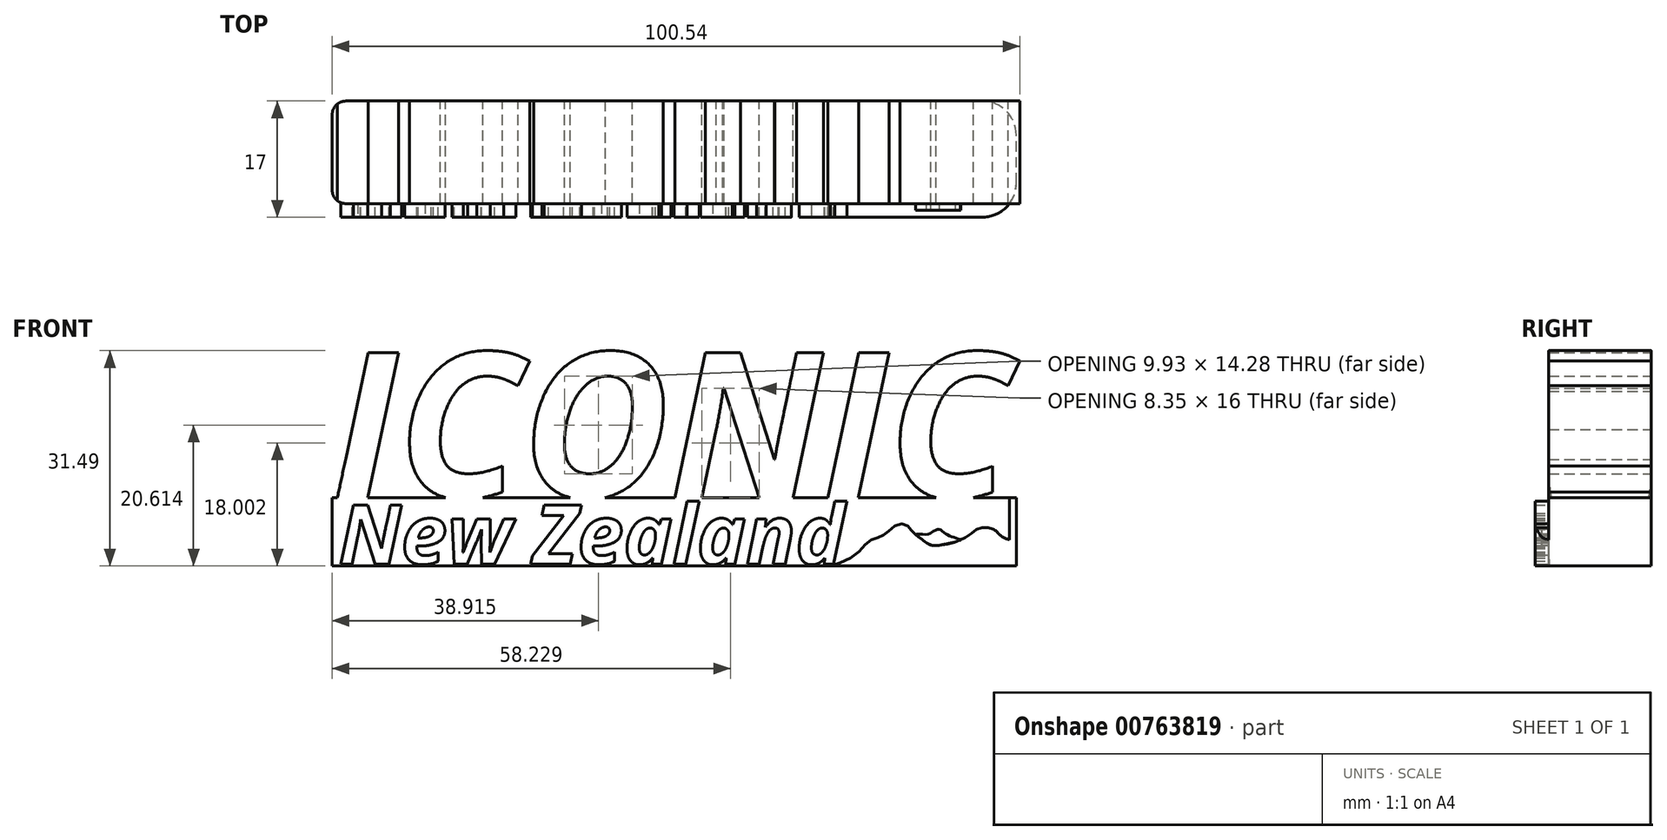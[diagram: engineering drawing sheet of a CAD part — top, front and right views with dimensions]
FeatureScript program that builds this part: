
annotation { "Feature Type Name" : "Feature", "Feature Type Description" : "" }
export const myFeature = defineFeature(function(context is Context, id is Id, definition is map)
    precondition{}
    {
        {
            var Q0;
            Q0=qCreatedBy(makeId("Front.planeOp"),FACE);
            var sketch = newSketch(context, id + "F0", { "sketchPlane" : qUnion([Q0])});
            skLineSegment(sketch, "E0.bottom", {"start": v(-50, 5) * mm, "end": v(50, 5) * mm});
            skLineSegment(sketch, "E0.top", {"start": v(-50, -5) * mm, "end": v(50, -5) * mm});
            skLineSegment(sketch, "E0.left", {"start": v(-50, 5) * mm, "end": v(-50, -5) * mm});
            skLineSegment(sketch, "E0.right", {"start": v(50, 5) * mm, "end": v(50, -5) * mm});
            skPoint(sketch, "E0.middle", {"position": v(0, 0) * mm});
            skText(sketch, "E1", { "text": "ICONIC", "fontName": "OpenSans-BoldItalic.ttf"});
            const initialGuessF0  = {"E1": [-0.05, 0.005, 1, 0, 0.02134]};
            skSetInitialGuess(sketch, initialGuessF0);
            skSolve(sketch);
        }
        {
            var Q0;
            Q0 = qSketchRegion(id + "F0", true);
            extrude(context, id + "F1", {"entities" : qUnion([Q0]), "depth" : 15 * mm, "offsetDistance" : 25 * mm});
        }
        {
            var Q0;
            Q0=makeQuery(id+"F1.opExtrude","CAP_FACE",FACE,{"disambiguationData":[OSD([sQuery(id+"F0.wireOp",EDGE,"E0.bottom"),sQuery(id+"F0.wireOp",EDGE,"E0.top"),sQuery(id+"F0.wireOp",EDGE,"E0.left"),sQuery(id+"F0.wireOp",EDGE,"E0.right"),sQuery(id+"F0.wireOp",EDGE,"E1.sketch_text.stroke-0"),sQuery(id+"F0.wireOp",EDGE,"E1.sketch_text.stroke-1"),sQuery(id+"F0.wireOp",EDGE,"E1.sketch_text.stroke-2"),sQuery(id+"F0.wireOp",EDGE,"E1.sketch_text.stroke-4"),sQuery(id+"F0.wireOp",EDGE,"E1.sketch_text.stroke-5"),sQuery(id+"F0.wireOp",EDGE,"E1.sketch_text.stroke-6"),sQuery(id+"F0.wireOp",EDGE,"E1.sketch_text.stroke-7"),sQuery(id+"F0.wireOp",EDGE,"E1.sketch_text.stroke-8"),sQuery(id+"F0.wireOp",EDGE,"E1.sketch_text.stroke-9"),sQuery(id+"F0.wireOp",EDGE,"E1.sketch_text.stroke-10"),sQuery(id+"F0.wireOp",EDGE,"E1.sketch_text.stroke-11"),sQuery(id+"F0.wireOp",EDGE,"E1.sketch_text.stroke-12"),sQuery(id+"F0.wireOp",EDGE,"E1.sketch_text.stroke-13"),sQuery(id+"F0.wireOp",EDGE,"E1.sketch_text.stroke-14"),sQuery(id+"F0.wireOp",EDGE,"E1.sketch_text.stroke-15"),sQuery(id+"F0.wireOp",EDGE,"E1.sketch_text.stroke-16"),sQuery(id+"F0.wireOp",EDGE,"E1.sketch_text.stroke-17"),sQuery(id+"F0.wireOp",EDGE,"E1.sketch_text.stroke-18"),sQuery(id+"F0.wireOp",EDGE,"E1.sketch_text.stroke-19"),sQuery(id+"F0.wireOp",EDGE,"E1.sketch_text.stroke-20"),sQuery(id+"F0.wireOp",EDGE,"E1.sketch_text.stroke-21"),sQuery(id+"F0.wireOp",EDGE,"E1.sketch_text.stroke-22"),sQuery(id+"F0.wireOp",EDGE,"E1.sketch_text.stroke-23"),sQuery(id+"F0.wireOp",EDGE,"E1.sketch_text.stroke-24"),sQuery(id+"F0.wireOp",EDGE,"E1.sketch_text.stroke-25"),sQuery(id+"F0.wireOp",EDGE,"E1.sketch_text.stroke-26"),sQuery(id+"F0.wireOp",EDGE,"E1.sketch_text.stroke-27"),sQuery(id+"F0.wireOp",EDGE,"E1.sketch_text.stroke-28"),sQuery(id+"F0.wireOp",EDGE,"E1.sketch_text.stroke-29"),sQuery(id+"F0.wireOp",EDGE,"E1.sketch_text.stroke-30"),sQuery(id+"F0.wireOp",EDGE,"E1.sketch_text.stroke-31"),sQuery(id+"F0.wireOp",EDGE,"E1.sketch_text.stroke-32"),sQuery(id+"F0.wireOp",EDGE,"E1.sketch_text.stroke-33"),sQuery(id+"F0.wireOp",EDGE,"E1.sketch_text.stroke-34"),sQuery(id+"F0.wireOp",EDGE,"E1.sketch_text.stroke-35"),sQuery(id+"F0.wireOp",EDGE,"E1.sketch_text.stroke-36"),sQuery(id+"F0.wireOp",EDGE,"E1.sketch_text.stroke-37"),sQuery(id+"F0.wireOp",EDGE,"E1.sketch_text.stroke-38"),sQuery(id+"F0.wireOp",EDGE,"E1.sketch_text.stroke-39"),sQuery(id+"F0.wireOp",EDGE,"E1.sketch_text.stroke-40"),sQuery(id+"F0.wireOp",EDGE,"E1.sketch_text.stroke-41"),sQuery(id+"F0.wireOp",EDGE,"E1.sketch_text.stroke-43"),sQuery(id+"F0.wireOp",EDGE,"E1.sketch_text.stroke-44"),sQuery(id+"F0.wireOp",EDGE,"E1.sketch_text.stroke-45"),sQuery(id+"F0.wireOp",EDGE,"E1.sketch_text.stroke-46"),sQuery(id+"F0.wireOp",EDGE,"E1.sketch_text.stroke-47"),sQuery(id+"F0.wireOp",EDGE,"E1.sketch_text.stroke-49"),sQuery(id+"F0.wireOp",EDGE,"E1.sketch_text.stroke-50"),sQuery(id+"F0.wireOp",EDGE,"E1.sketch_text.stroke-51"),sQuery(id+"F0.wireOp",EDGE,"E1.sketch_text.stroke-52"),sQuery(id+"F0.wireOp",EDGE,"E1.sketch_text.stroke-53"),sQuery(id+"F0.wireOp",EDGE,"E1.sketch_text.stroke-54"),sQuery(id+"F0.wireOp",EDGE,"E1.sketch_text.stroke-55"),sQuery(id+"F0.wireOp",EDGE,"E1.sketch_text.stroke-56"),sQuery(id+"F0.wireOp",EDGE,"E1.sketch_text.stroke-57"),sQuery(id+"F0.wireOp",EDGE,"E1.sketch_text.stroke-58"),sQuery(id+"F0.wireOp",EDGE,"E1.sketch_text.stroke-59"),sQuery(id+"F0.wireOp",EDGE,"E1.sketch_text.stroke-61"),sQuery(id+"F0.wireOp",EDGE,"E1.sketch_text.stroke-62"),sQuery(id+"F0.wireOp",EDGE,"E1.sketch_text.stroke-63"),sQuery(id+"F0.wireOp",EDGE,"E1.sketch_text.stroke-64"),sQuery(id+"F0.wireOp",EDGE,"E1.sketch_text.stroke-65"),sQuery(id+"F0.wireOp",EDGE,"E1.sketch_text.stroke-66"),sQuery(id+"F0.wireOp",EDGE,"E1.sketch_text.stroke-67"),sQuery(id+"F0.wireOp",EDGE,"E1.sketch_text.stroke-68"),sQuery(id+"F0.wireOp",EDGE,"E1.sketch_text.stroke-69"),sQuery(id+"F0.wireOp",EDGE,"E1.sketch_text.stroke-70"),sQuery(id+"F0.wireOp",EDGE,"E1.sketch_text.stroke-71"),sQuery(id+"F0.wireOp",EDGE,"E1.sketch_text.stroke-72"),sQuery(id+"F0.wireOp",EDGE,"E1.sketch_text.stroke-73"),sQuery(id+"F0.wireOp",EDGE,"E1.sketch_text.stroke-74"),sQuery(id+"F0.wireOp",EDGE,"E1.sketch_text.stroke-75"),sQuery(id+"F0.wireOp",EDGE,"E1.sketch_text.stroke-76"),sQuery(id+"F0.wireOp",EDGE,"E1.sketch_text.stroke-77"),sQuery(id+"F0.wireOp",EDGE,"E1.sketch_text.stroke-78")])],"isStart":false});
            var sketch = newSketch(context, id + "F2", { "sketchPlane" : qUnion([Q0])});
            skText(sketch, "E2", { "text": "New Zealand", "fontName": "OpenSans-BoldItalic.ttf"});
            const initialGuessF2  = {"E2": [-0.04902, -0.00471, 1, 0, 0.00867]};
            skSetInitialGuess(sketch, initialGuessF2);
            skSolve(sketch);
        }
        {
            var Q0;
            Q0 = qSketchRegion(id + "F2", true);
            extrude(context, id + "F3", {"entities" : qUnion([Q0]), "operationType" : NewBodyOperationType.ADD, "depth" : 2 * mm, "offsetDistance" : 25 * mm});
        }
        {
            var Q0;
            {var subQ0=sQuery(id+"F0.wireOp",EDGE,"E1.sketch_text.stroke-34");var subQ1=sQuery(id+"F0.wireOp",EDGE,"E1.sketch_text.stroke-33");var subQ2=sQuery(id+"F0.wireOp",EDGE,"E1.sketch_text.stroke-32");var subQ3=sQuery(id+"F0.wireOp",EDGE,"E1.sketch_text.stroke-55");var subQ4=sQuery(id+"F0.wireOp",EDGE,"E1.sketch_text.stroke-31");var subQ5=sQuery(id+"F0.wireOp",EDGE,"E1.sketch_text.stroke-54");var subQ6=sQuery(id+"F0.wireOp",EDGE,"E1.sketch_text.stroke-30");var subQ7=sQuery(id+"F0.wireOp",EDGE,"E1.sketch_text.stroke-53");var subQ8=sQuery(id+"F0.wireOp",EDGE,"E1.sketch_text.stroke-29");var subQ9=sQuery(id+"F0.wireOp",EDGE,"E1.sketch_text.stroke-52");var subQ10=sQuery(id+"F0.wireOp",EDGE,"E1.sketch_text.stroke-28");var subQ11=sQuery(id+"F0.wireOp",EDGE,"E1.sketch_text.stroke-51");var subQ12=sQuery(id+"F0.wireOp",EDGE,"E1.sketch_text.stroke-27");var subQ13=sQuery(id+"F0.wireOp",EDGE,"E1.sketch_text.stroke-17");var subQ14=sQuery(id+"F0.wireOp",EDGE,"E1.sketch_text.stroke-26");var subQ15=sQuery(id+"F0.wireOp",EDGE,"E1.sketch_text.stroke-50");var subQ16=sQuery(id+"F0.wireOp",EDGE,"E1.sketch_text.stroke-16");var subQ17=sQuery(id+"F0.wireOp",EDGE,"E1.sketch_text.stroke-25");var subQ18=sQuery(id+"F0.wireOp",EDGE,"E1.sketch_text.stroke-49");var subQ19=sQuery(id+"F0.wireOp",EDGE,"E1.sketch_text.stroke-24");var subQ20=sQuery(id+"F0.wireOp",EDGE,"E1.sketch_text.stroke-47");var subQ21=sQuery(id+"F0.wireOp",EDGE,"E1.sketch_text.stroke-14");var subQ22=sQuery(id+"F0.wireOp",EDGE,"E1.sketch_text.stroke-23");var subQ23=sQuery(id+"F0.wireOp",EDGE,"E1.sketch_text.stroke-46");var subQ24=sQuery(id+"F0.wireOp",EDGE,"E1.sketch_text.stroke-13");var subQ25=sQuery(id+"F0.wireOp",EDGE,"E1.sketch_text.stroke-22");var subQ26=sQuery(id+"F0.wireOp",EDGE,"E1.sketch_text.stroke-45");var subQ27=sQuery(id+"F0.wireOp",EDGE,"E1.sketch_text.stroke-12");var subQ28=sQuery(id+"F0.wireOp",EDGE,"E1.sketch_text.stroke-21");var subQ29=sQuery(id+"F0.wireOp",EDGE,"E1.sketch_text.stroke-44");var subQ30=sQuery(id+"F0.wireOp",EDGE,"E0.top");var subQ31=sQuery(id+"F0.wireOp",EDGE,"E0.right");var subQ32=sQuery(id+"F0.wireOp",EDGE,"E0.bottom");var subQ33=sQuery(id+"F0.wireOp",EDGE,"E1.sketch_text.stroke-68");var subQ35=sQuery(id+"F0.wireOp",EDGE,"E1.sketch_text.stroke-59");var subQ36=sQuery(id+"F0.wireOp",EDGE,"E1.sketch_text.stroke-69");var subQ37=sQuery(id+"F0.wireOp",EDGE,"E1.sketch_text.stroke-56");var subQ39=sQuery(id+"F0.wireOp",EDGE,"E1.sketch_text.stroke-57");var subQ40=sQuery(id+"F0.wireOp",EDGE,"E1.sketch_text.stroke-43");var subQ42=sQuery(id+"F0.wireOp",EDGE,"E0.left");var subQ43=sQuery(id+"F0.wireOp",EDGE,"E1.sketch_text.stroke-35");var subQ45=sQuery(id+"F0.wireOp",EDGE,"E1.sketch_text.stroke-0");var subQ46=sQuery(id+"F0.wireOp",EDGE,"E1.sketch_text.stroke-11");var subQ47=sQuery(id+"F0.wireOp",EDGE,"E1.sketch_text.stroke-20");var subQ48=sQuery(id+"F0.wireOp",EDGE,"E1.sketch_text.stroke-2");var subQ49=sQuery(id+"F0.wireOp",EDGE,"E1.sketch_text.stroke-1");var subQ50=sQuery(id+"F0.wireOp",EDGE,"E1.sketch_text.stroke-4");var subQ51=sQuery(id+"F0.wireOp",EDGE,"E1.sketch_text.stroke-5");var subQ52=sQuery(id+"F0.wireOp",EDGE,"E1.sketch_text.stroke-6");var subQ53=sQuery(id+"F0.wireOp",EDGE,"E1.sketch_text.stroke-15");var subQ54=sQuery(id+"F0.wireOp",EDGE,"E1.sketch_text.stroke-37");var subQ55=sQuery(id+"F0.wireOp",EDGE,"E1.sketch_text.stroke-7");var subQ56=sQuery(id+"F0.wireOp",EDGE,"E1.sketch_text.stroke-8");var subQ57=sQuery(id+"F0.wireOp",EDGE,"E1.sketch_text.stroke-9");var subQ58=sQuery(id+"F0.wireOp",EDGE,"E1.sketch_text.stroke-18");var subQ59=sQuery(id+"F0.wireOp",EDGE,"E1.sketch_text.stroke-40");var subQ60=sQuery(id+"F0.wireOp",EDGE,"E1.sketch_text.stroke-10");var subQ61=sQuery(id+"F0.wireOp",EDGE,"E1.sketch_text.stroke-19");var subQ62=sQuery(id+"F0.wireOp",EDGE,"E1.sketch_text.stroke-41");var subQ63=sQuery(id+"F0.wireOp",EDGE,"E1.sketch_text.stroke-36");var subQ64=sQuery(id+"F0.wireOp",EDGE,"E1.sketch_text.stroke-38");var subQ65=sQuery(id+"F0.wireOp",EDGE,"E1.sketch_text.stroke-39");var subQ66=sQuery(id+"F0.wireOp",EDGE,"E1.sketch_text.stroke-65");var subQ67=sQuery(id+"F0.wireOp",EDGE,"E1.sketch_text.stroke-66");var subQ68=sQuery(id+"F0.wireOp",EDGE,"E1.sketch_text.stroke-67");var subQ69=sQuery(id+"F0.wireOp",EDGE,"E1.sketch_text.stroke-70");var subQ70=sQuery(id+"F0.wireOp",EDGE,"E1.sketch_text.stroke-71");var subQ71=sQuery(id+"F0.wireOp",EDGE,"E1.sketch_text.stroke-72");var subQ72=sQuery(id+"F0.wireOp",EDGE,"E1.sketch_text.stroke-73");var subQ73=sQuery(id+"F0.wireOp",EDGE,"E1.sketch_text.stroke-74");var subQ74=sQuery(id+"F0.wireOp",EDGE,"E1.sketch_text.stroke-75");var subQ75=sQuery(id+"F0.wireOp",EDGE,"E1.sketch_text.stroke-76");var subQ76=sQuery(id+"F0.wireOp",EDGE,"E1.sketch_text.stroke-77");var subQ77=sQuery(id+"F0.wireOp",EDGE,"E1.sketch_text.stroke-78");var subQ78=sQuery(id+"F0.wireOp",EDGE,"E1.sketch_text.stroke-58");var subQ79=sQuery(id+"F0.wireOp",EDGE,"E1.sketch_text.stroke-61");var subQ80=sQuery(id+"F0.wireOp",EDGE,"E1.sketch_text.stroke-62");var subQ81=sQuery(id+"F0.wireOp",EDGE,"E1.sketch_text.stroke-63");var subQ82=sQuery(id+"F0.wireOp",EDGE,"E1.sketch_text.stroke-64");Q0=makeQuery(id+"F3.boolean.opBoolean","SPLIT",FACE,{"disambiguationData":[TD([makeQuery(id+"F1.opExtrude","SWEPT_FACE",FACE,{"disambiguationData":[OSD([subQ30])]})])],"derivedFrom":makeQuery(id+"F1.opExtrude","CAP_FACE",FACE,{"disambiguationData":[OSD([subQ32,subQ30,subQ42,subQ31,subQ45,subQ49,subQ48,subQ50,subQ51,subQ52,subQ55,subQ56,subQ57,subQ60,subQ46,subQ27,subQ24,subQ21,subQ53,subQ16,subQ13,subQ58,subQ61,subQ47,subQ28,subQ25,subQ22,subQ19,subQ17,subQ14,subQ12,subQ10,subQ8,subQ6,subQ4,subQ2,subQ1,subQ0,subQ43,subQ63,subQ54,subQ64,subQ65,subQ59,subQ62,subQ40,subQ29,subQ26,subQ23,subQ20,subQ18,subQ15,subQ11,subQ9,subQ7,subQ5,subQ3,subQ37,subQ39,subQ78,subQ35,subQ79,subQ80,subQ81,subQ82,subQ66,subQ67,subQ68,subQ33,subQ36,subQ69,subQ70,subQ71,subQ72,subQ73,subQ74,subQ75,subQ76,subQ77])],"isStart":false})});}
            var sketch = newSketch(context, id + "F4", { "sketchPlane" : qUnion([Q0])});
            skFitSpline(sketch, "E3", {"points": [v(22.82, -5) * mm, v(26.5, -3.3) * mm, v(28.51, -1.35) * mm, v(30.03, -0.76) * mm, v(31.19, 0) * mm, v(32.84, 1.12) * mm, v(34.25, 0.73) * mm, v(34.78, 0) * mm, v(36.07, -1.02) * mm, v(37.39, -1.91) * mm, v(39, -1.94) * mm, v(41.84, -1.22) * mm, v(43.79, 0) * mm, v(44.71, 0.56) * mm, v(46.76, 0.3) * mm, v(47.81, -0.66) * mm, v(50, -1.38) * mm], "startDerivative": vector(35.27, 6.8) * mm, "endDerivative": vector(35.57, -7.54) * mm});
            skLineSegment(sketch, "E4", {"start": v(22.82, -5) * mm, "end": v(50, -5) * mm});
            skLineSegment(sketch, "E5", {"start": v(50, -5) * mm, "end": v(50, -1.38) * mm});
            skSolve(sketch);
        }
        {
            var Q0;
            Q0 = qSketchRegion(id + "F4", true);
            extrude(context, id + "F5", {"entities" : qUnion([Q0]), "operationType" : NewBodyOperationType.ADD, "depth" : 2 * mm, "offsetDistance" : 25 * mm});
        }
        {
            var Q0;
            {var subQ0=sQuery(id+"F0.wireOp",EDGE,"E1.sketch_text.stroke-34");var subQ1=sQuery(id+"F0.wireOp",EDGE,"E1.sketch_text.stroke-33");var subQ2=sQuery(id+"F0.wireOp",EDGE,"E1.sketch_text.stroke-32");var subQ3=sQuery(id+"F0.wireOp",EDGE,"E1.sketch_text.stroke-55");var subQ4=sQuery(id+"F0.wireOp",EDGE,"E1.sketch_text.stroke-31");var subQ5=sQuery(id+"F0.wireOp",EDGE,"E1.sketch_text.stroke-54");var subQ6=sQuery(id+"F0.wireOp",EDGE,"E1.sketch_text.stroke-30");var subQ7=sQuery(id+"F0.wireOp",EDGE,"E1.sketch_text.stroke-53");var subQ8=sQuery(id+"F0.wireOp",EDGE,"E1.sketch_text.stroke-29");var subQ9=sQuery(id+"F0.wireOp",EDGE,"E1.sketch_text.stroke-52");var subQ10=sQuery(id+"F0.wireOp",EDGE,"E1.sketch_text.stroke-28");var subQ11=sQuery(id+"F0.wireOp",EDGE,"E1.sketch_text.stroke-51");var subQ12=sQuery(id+"F0.wireOp",EDGE,"E1.sketch_text.stroke-27");var subQ13=sQuery(id+"F0.wireOp",EDGE,"E1.sketch_text.stroke-17");var subQ14=sQuery(id+"F0.wireOp",EDGE,"E1.sketch_text.stroke-26");var subQ15=sQuery(id+"F0.wireOp",EDGE,"E1.sketch_text.stroke-50");var subQ16=sQuery(id+"F0.wireOp",EDGE,"E1.sketch_text.stroke-16");var subQ17=sQuery(id+"F0.wireOp",EDGE,"E1.sketch_text.stroke-25");var subQ18=sQuery(id+"F0.wireOp",EDGE,"E1.sketch_text.stroke-49");var subQ19=sQuery(id+"F0.wireOp",EDGE,"E1.sketch_text.stroke-24");var subQ20=sQuery(id+"F0.wireOp",EDGE,"E1.sketch_text.stroke-47");var subQ21=sQuery(id+"F0.wireOp",EDGE,"E1.sketch_text.stroke-14");var subQ22=sQuery(id+"F0.wireOp",EDGE,"E1.sketch_text.stroke-23");var subQ23=sQuery(id+"F0.wireOp",EDGE,"E1.sketch_text.stroke-46");var subQ24=sQuery(id+"F0.wireOp",EDGE,"E1.sketch_text.stroke-13");var subQ25=sQuery(id+"F0.wireOp",EDGE,"E1.sketch_text.stroke-22");var subQ26=sQuery(id+"F0.wireOp",EDGE,"E1.sketch_text.stroke-45");var subQ27=sQuery(id+"F0.wireOp",EDGE,"E1.sketch_text.stroke-12");var subQ28=sQuery(id+"F0.wireOp",EDGE,"E1.sketch_text.stroke-21");var subQ29=sQuery(id+"F0.wireOp",EDGE,"E1.sketch_text.stroke-44");var subQ30=sQuery(id+"F0.wireOp",EDGE,"E0.top");var subQ31=sQuery(id+"F0.wireOp",EDGE,"E0.right");var subQ32=sQuery(id+"F0.wireOp",EDGE,"E0.bottom");var subQ33=sQuery(id+"F0.wireOp",EDGE,"E1.sketch_text.stroke-68");var subQ35=sQuery(id+"F0.wireOp",EDGE,"E1.sketch_text.stroke-59");var subQ36=sQuery(id+"F0.wireOp",EDGE,"E1.sketch_text.stroke-69");var subQ37=sQuery(id+"F0.wireOp",EDGE,"E1.sketch_text.stroke-56");var subQ39=sQuery(id+"F0.wireOp",EDGE,"E1.sketch_text.stroke-57");var subQ40=sQuery(id+"F0.wireOp",EDGE,"E1.sketch_text.stroke-43");var subQ42=sQuery(id+"F0.wireOp",EDGE,"E0.left");var subQ43=sQuery(id+"F0.wireOp",EDGE,"E1.sketch_text.stroke-35");var subQ45=sQuery(id+"F0.wireOp",EDGE,"E1.sketch_text.stroke-0");var subQ46=sQuery(id+"F0.wireOp",EDGE,"E1.sketch_text.stroke-11");var subQ47=sQuery(id+"F0.wireOp",EDGE,"E1.sketch_text.stroke-20");var subQ48=sQuery(id+"F0.wireOp",EDGE,"E1.sketch_text.stroke-2");var subQ49=sQuery(id+"F0.wireOp",EDGE,"E1.sketch_text.stroke-1");var subQ50=sQuery(id+"F0.wireOp",EDGE,"E1.sketch_text.stroke-4");var subQ51=sQuery(id+"F0.wireOp",EDGE,"E1.sketch_text.stroke-5");var subQ52=sQuery(id+"F0.wireOp",EDGE,"E1.sketch_text.stroke-6");var subQ53=sQuery(id+"F0.wireOp",EDGE,"E1.sketch_text.stroke-15");var subQ54=sQuery(id+"F0.wireOp",EDGE,"E1.sketch_text.stroke-37");var subQ55=sQuery(id+"F0.wireOp",EDGE,"E1.sketch_text.stroke-7");var subQ56=sQuery(id+"F0.wireOp",EDGE,"E1.sketch_text.stroke-8");var subQ57=sQuery(id+"F0.wireOp",EDGE,"E1.sketch_text.stroke-9");var subQ58=sQuery(id+"F0.wireOp",EDGE,"E1.sketch_text.stroke-18");var subQ59=sQuery(id+"F0.wireOp",EDGE,"E1.sketch_text.stroke-40");var subQ60=sQuery(id+"F0.wireOp",EDGE,"E1.sketch_text.stroke-10");var subQ61=sQuery(id+"F0.wireOp",EDGE,"E1.sketch_text.stroke-19");var subQ62=sQuery(id+"F0.wireOp",EDGE,"E1.sketch_text.stroke-41");var subQ63=sQuery(id+"F0.wireOp",EDGE,"E1.sketch_text.stroke-36");var subQ64=sQuery(id+"F0.wireOp",EDGE,"E1.sketch_text.stroke-38");var subQ65=sQuery(id+"F0.wireOp",EDGE,"E1.sketch_text.stroke-39");var subQ66=sQuery(id+"F0.wireOp",EDGE,"E1.sketch_text.stroke-65");var subQ67=sQuery(id+"F0.wireOp",EDGE,"E1.sketch_text.stroke-66");var subQ68=sQuery(id+"F0.wireOp",EDGE,"E1.sketch_text.stroke-67");var subQ69=sQuery(id+"F0.wireOp",EDGE,"E1.sketch_text.stroke-70");var subQ70=sQuery(id+"F0.wireOp",EDGE,"E1.sketch_text.stroke-71");var subQ71=sQuery(id+"F0.wireOp",EDGE,"E1.sketch_text.stroke-72");var subQ72=sQuery(id+"F0.wireOp",EDGE,"E1.sketch_text.stroke-73");var subQ73=sQuery(id+"F0.wireOp",EDGE,"E1.sketch_text.stroke-74");var subQ74=sQuery(id+"F0.wireOp",EDGE,"E1.sketch_text.stroke-75");var subQ75=sQuery(id+"F0.wireOp",EDGE,"E1.sketch_text.stroke-76");var subQ76=sQuery(id+"F0.wireOp",EDGE,"E1.sketch_text.stroke-77");var subQ77=sQuery(id+"F0.wireOp",EDGE,"E1.sketch_text.stroke-78");var subQ78=sQuery(id+"F0.wireOp",EDGE,"E1.sketch_text.stroke-58");var subQ79=sQuery(id+"F0.wireOp",EDGE,"E1.sketch_text.stroke-61");var subQ80=sQuery(id+"F0.wireOp",EDGE,"E1.sketch_text.stroke-62");var subQ81=sQuery(id+"F0.wireOp",EDGE,"E1.sketch_text.stroke-63");var subQ82=sQuery(id+"F0.wireOp",EDGE,"E1.sketch_text.stroke-64");Q0=makeQuery(id+"F3.boolean.opBoolean","SPLIT",FACE,{"disambiguationData":[TD([makeQuery(id+"F1.opExtrude","SWEPT_FACE",FACE,{"disambiguationData":[OSD([subQ30])]})])],"derivedFrom":makeQuery(id+"F1.opExtrude","CAP_FACE",FACE,{"disambiguationData":[OSD([subQ32,subQ30,subQ42,subQ31,subQ45,subQ49,subQ48,subQ50,subQ51,subQ52,subQ55,subQ56,subQ57,subQ60,subQ46,subQ27,subQ24,subQ21,subQ53,subQ16,subQ13,subQ58,subQ61,subQ47,subQ28,subQ25,subQ22,subQ19,subQ17,subQ14,subQ12,subQ10,subQ8,subQ6,subQ4,subQ2,subQ1,subQ0,subQ43,subQ63,subQ54,subQ64,subQ65,subQ59,subQ62,subQ40,subQ29,subQ26,subQ23,subQ20,subQ18,subQ15,subQ11,subQ9,subQ7,subQ5,subQ3,subQ37,subQ39,subQ78,subQ35,subQ79,subQ80,subQ81,subQ82,subQ66,subQ67,subQ68,subQ33,subQ36,subQ69,subQ70,subQ71,subQ72,subQ73,subQ74,subQ75,subQ76,subQ77])],"isStart":false})});}
            var sketch = newSketch(context, id + "F6", { "sketchPlane" : qUnion([Q0])});
            skFitSpline(sketch, "E6", {"points": [v(35.27, -0.44) * mm, v(36.8, -0.4) * mm, v(37.77, 0) * mm, v(38.66, 0.35) * mm, v(39.27, 0) * mm, v(40.21, -0.59) * mm, v(41.46, -1) * mm, v(41.84, -1.22) * mm, v(38.77, -1.98) * mm, v(37.5, -1.95) * mm, v(35.27, -0.44) * mm]});
            skSolve(sketch);
        }
        {
            var Q0;
            Q0 = qSketchRegion(id + "F6", true);
            extrude(context, id + "F7", {"entities" : qUnion([Q0]), "operationType" : NewBodyOperationType.ADD, "depth" : 1 * mm, "offsetDistance" : 25 * mm});
        }
        {
            var Q0;
            Q0=makeQuery(id+"F5.opExtrude","CAP_EDGE",EDGE,{"disambiguationData":[OSD([sQuery(id+"F4.wireOp",EDGE,"E5")])],"isStart":false});
            var Q1;
            Q1=makeQuery(id+"F1.opExtrude","CAP_EDGE",EDGE,{"disambiguationData":[OSD([sQuery(id+"F0.wireOp",EDGE,"E0.right")])],"isStart":true});
            fillet(context, id + "F8", {"entities" : qUnion([Q0, Q1]), "radius" : 5 * mm, "tangentPropagation" : true, "allowEdgeOverflow" : false});
        }
        {
            var Q0;
            Q0=makeQuery(id+"F1.opExtrude","CAP_EDGE",EDGE,{"disambiguationData":[OSD([sQuery(id+"F0.wireOp",EDGE,"E0.left")])],"isStart":false});
            var Q1;
            Q1=makeQuery(id+"F1.opExtrude","CAP_EDGE",EDGE,{"disambiguationData":[OSD([sQuery(id+"F0.wireOp",EDGE,"E0.left")])],"isStart":true});
            fillet(context, id + "F9", {"entities" : qUnion([Q0, Q1]), "radius" : 2 * mm, "tangentPropagation" : true, "allowEdgeOverflow" : false});
        }
    });
